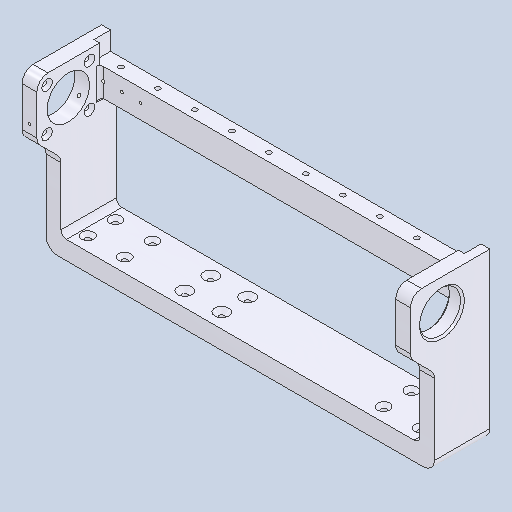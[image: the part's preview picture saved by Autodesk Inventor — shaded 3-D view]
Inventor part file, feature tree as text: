
AUTODESK INVENTOR PART (.ipt)
format: ipt  version: 2024.1 (Build 281209000, 209)  size: 265,216 bytes
history: native  units: mm
features: sketch x4, other x3, extrude x1
ambient origin geometry x8: Origin, YZ Plane, XZ Plane, XY Plane, X Axis, Y Axis, Z Axis, Center Point
bodies: Solid1 (feature_tree)
feature tree (8):
  other  "gantry_L.ipt"
  extrude  "Extrusion1"  Depth=10.0mm
  other  "Solid1::gantry_L.ipt"
  other  "TaggingFeature1"
  sketch  "Sketch1"  dims[d0=10.0mm d1=1.6mm]
  sketch  "Sketch2"  dims[d2=1.6mm]
  sketch  "Sketch3"  dims[d3=1.6mm]
  sketch  "Sketch16"  dims[d4=1.6mm d5=4.0mm d6=13.0mm d7=7.0mm d8=10.0mm d9=7.0mm d10=7.0mm d11=10.0mm d12=10.0mm d13=0.0mm d14=0.0mm]
